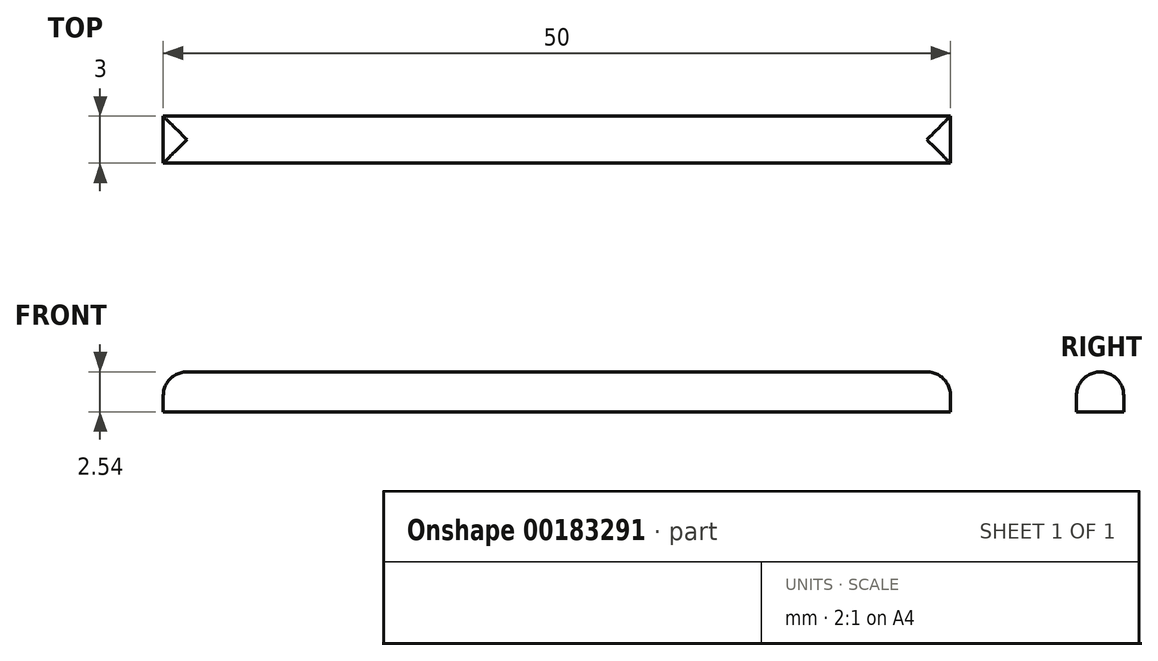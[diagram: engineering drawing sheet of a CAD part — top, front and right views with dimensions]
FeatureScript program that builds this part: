
annotation { "Feature Type Name" : "Feature", "Feature Type Description" : "" }
export const myFeature = defineFeature(function(context is Context, id is Id, definition is map)
    precondition{}
    {
        {
            var Q0;
            Q0=qCreatedBy(makeId("Top.planeOp"),FACE);
            var sketch = newSketch(context, id + "F0", { "sketchPlane" : qUnion([Q0])});
            skLineSegment(sketch, "E0.bottom", {"start": v(25, 1.5) * mm, "end": v(-25, 1.5) * mm});
            skLineSegment(sketch, "E0.top", {"start": v(25, -1.5) * mm, "end": v(-25, -1.5) * mm});
            skLineSegment(sketch, "E0.left", {"start": v(25, 1.5) * mm, "end": v(25, -1.5) * mm});
            skLineSegment(sketch, "E0.right", {"start": v(-25, 1.5) * mm, "end": v(-25, -1.5) * mm});
            skPoint(sketch, "E0.middle", {"position": v(0, 0) * mm});
            skSolve(sketch);
        }
        {
            var Q0;
            Q0=makeQuery(id+"F0.imprint","IMPRINT",FACE,{"disambiguationData":[TD([[makeQuery(id+"F0.imprint","IMPRINT",EDGE,{"derivedFrom":sQuery(id+"F0.wireOp",EDGE,"E0.bottom")}),1.0]])]});
            extrude(context, id + "F1", {"entities" : qUnion([Q0]), "depth" : 2.54 * mm});
        }
        {
            var Q0;
            Q0=makeQuery(id+"F1.opExtrude","CAP_FACE",FACE,{"disambiguationData":[OSD([sQuery(id+"F0.wireOp",EDGE,"E0.bottom"),sQuery(id+"F0.wireOp",EDGE,"E0.top"),sQuery(id+"F0.wireOp",EDGE,"E0.left"),sQuery(id+"F0.wireOp",EDGE,"E0.right")])],"isStart":false});
            fillet(context, id + "F2", {"entities" : qUnion([Q0]), "radius" : 1.5 * mm, "tangentPropagation" : true, "allowEdgeOverflow" : false});
        }
    });
